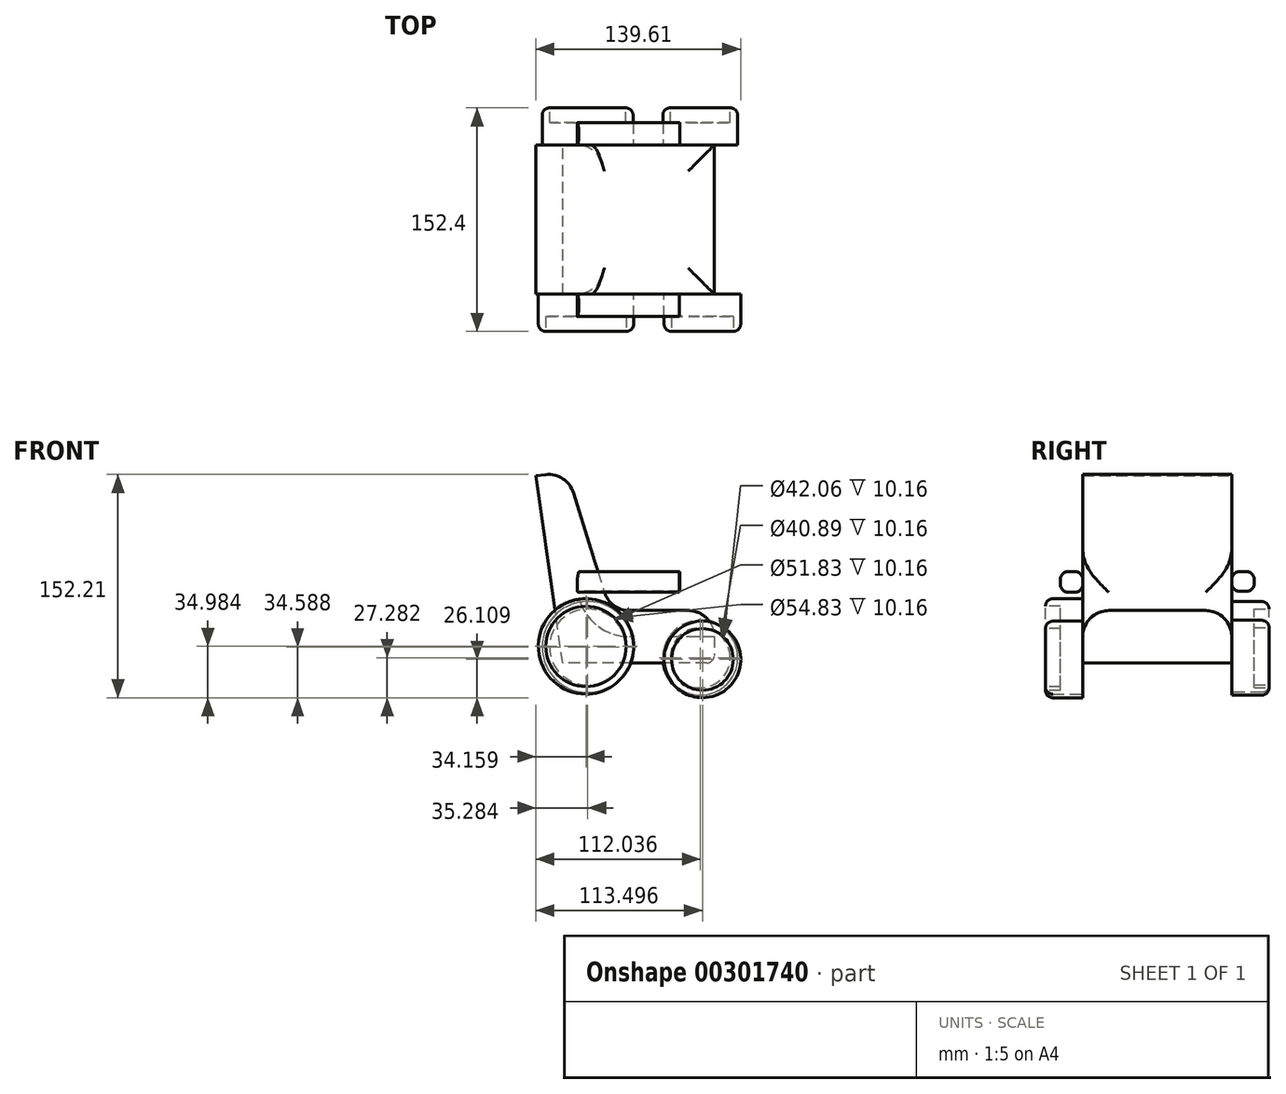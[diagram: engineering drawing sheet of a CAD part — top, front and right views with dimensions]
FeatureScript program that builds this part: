
annotation { "Feature Type Name" : "Feature", "Feature Type Description" : "" }
export const myFeature = defineFeature(function(context is Context, id is Id, definition is map)
    precondition{}
    {
        {
            var Q0;
            Q0=qCreatedBy(makeId("Front.planeOp"),FACE);
            var sketch = newSketch(context, id + "F0", { "sketchPlane" : qUnion([Q0])});
            skLineSegment(sketch, "E0", {"start": v(-41.82, 75.7) * mm, "end": v(-12.5, -18.42) * mm});
            skLineSegment(sketch, "E1", {"start": v(-12.5, -18.42) * mm, "end": v(58.5, -18.42) * mm});
            skLineSegment(sketch, "E2", {"start": v(58.5, -18.42) * mm, "end": v(58.5, -54.2) * mm});
            skLineSegment(sketch, "E3", {"start": v(58.5, -54.2) * mm, "end": v(-44.78, -54.2) * mm});
            skLineSegment(sketch, "E4", {"start": v(-44.78, -54.2) * mm, "end": v(-63.07, 73.56) * mm});
            skLineSegment(sketch, "E5", {"start": v(-63.07, 73.56) * mm, "end": v(-41.82, 75.7) * mm});
            skSolve(sketch);
        }
        {
            var Q0;
            Q0=makeQuery(id+"F0.imprint","IMPRINT",FACE,{"disambiguationData":[TD([[makeQuery(id+"F0.imprint","IMPRINT",EDGE,{"derivedFrom":sQuery(id+"F0.wireOp",EDGE,"E0")}),-1.0]])]});
            extrude(context, id + "F1", {"entities" : qUnion([Q0]), "depth" : 101.6 * mm});
        }
        {
            var Q0;
            Q0=makeQuery(id+"F1.opExtrude","SWEPT_EDGE",EDGE,{"disambiguationData":[OSD([sQuery(id+"F0.wireOp",EDGE,"E0"),sQuery(id+"F0.wireOp",EDGE,"E1")])]});
            var Q1;
            Q1=makeQuery(id+"F1.opExtrude","CAP_EDGE",EDGE,{"disambiguationData":[OSD([sQuery(id+"F0.wireOp",EDGE,"E1")])],"isStart":false});
            var Q2;
            Q2=makeQuery(id+"F1.opExtrude","CAP_EDGE",EDGE,{"disambiguationData":[OSD([sQuery(id+"F0.wireOp",EDGE,"E1")])],"isStart":true});
            var Q3;
            Q3=makeQuery(id+"F1.opExtrude","SWEPT_EDGE",EDGE,{"disambiguationData":[OSD([sQuery(id+"F0.wireOp",EDGE,"E1"),sQuery(id+"F0.wireOp",EDGE,"E2")])]});
            var Q4;
            Q4=makeQuery(id+"F1.opExtrude","SWEPT_EDGE",EDGE,{"disambiguationData":[OSD([sQuery(id+"F0.wireOp",EDGE,"E0"),sQuery(id+"F0.wireOp",EDGE,"E5")])]});
            fillet(context, id + "F2", {"entities" : qUnion([Q0, Q1, Q2, Q3, Q4]), "radius" : 17.78 * mm, "tangentPropagation" : true, "allowEdgeOverflow" : false});
        }
        {
            var Q0;
            Q0=qCreatedBy(makeId("Front.planeOp"),FACE);
            var sketch = newSketch(context, id + "F3", { "sketchPlane" : qUnion([Q0])});
            skCircle(sketch, "E6", {"center": v(-27.79, -43.3) * mm, "radius": 31 * mm});
            skCircle(sketch, "E7", {"center": v(48.97, -50.6) * mm, "radius": 25.53 * mm});
            skSolve(sketch);
        }
        {
            var Q0;
            Q0=makeQuery(id+"F3.imprint","IMPRINT",FACE,{"disambiguationData":[TD([[makeQuery(id+"F3.imprint","IMPRINT",EDGE,{"derivedFrom":sQuery(id+"F3.wireOp",EDGE,"E7")}),1.0]])]});
            var Q1;
            Q1=makeQuery(id+"F3.imprint","IMPRINT",FACE,{"disambiguationData":[TD([[makeQuery(id+"F3.imprint","IMPRINT",EDGE,{"derivedFrom":sQuery(id+"F3.wireOp",EDGE,"E6")}),1.0]])]});
            extrude(context, id + "F4", {"entities" : qUnion([Q0, Q1]), "operationType" : NewBodyOperationType.ADD, "oppositeDirection" : true, "depth" : 25.4 * mm});
        }
        {
            var Q0;
            Q0=makeQuery(id+"F1.opExtrude","CAP_FACE",FACE,{"disambiguationData":[OSD([sQuery(id+"F0.wireOp",EDGE,"E0"),sQuery(id+"F0.wireOp",EDGE,"E1"),sQuery(id+"F0.wireOp",EDGE,"E2"),sQuery(id+"F0.wireOp",EDGE,"E3"),sQuery(id+"F0.wireOp",EDGE,"E4"),sQuery(id+"F0.wireOp",EDGE,"E5")])],"isStart":false});
            var sketch = newSketch(context, id + "F5", { "sketchPlane" : qUnion([Q0])});
            skCircle(sketch, "E8", {"center": v(-28.91, -42.9) * mm, "radius": 32.5 * mm});
            skCircle(sketch, "E9", {"center": v(50.43, -51.77) * mm, "radius": 26.1 * mm});
            skSolve(sketch);
        }
        {
            var Q0;
            Q0 = qSketchRegion(id + "F5", true);
            extrude(context, id + "F6", {"entities" : qUnion([Q0]), "operationType" : NewBodyOperationType.ADD, "depth" : 25.4 * mm});
        }
        {
            var Q0;
            {var subQ1=sQuery(id+"F0.wireOp",EDGE,"E0");var subQ2=sQuery(id+"F0.wireOp",EDGE,"E5");var subQ3=sQuery(id+"F0.wireOp",EDGE,"E4");Q0=makeQuery(id+"F6.boolean.opBoolean","SPLIT",FACE,{"disambiguationData":[TD([makeQuery(id+"F1.opExtrude","SWEPT_FACE",FACE,{"disambiguationData":[OSD([subQ3])]})])],"derivedFrom":makeQuery(id+"F1.opExtrude","CAP_FACE",FACE,{"disambiguationData":[OSD([subQ1,sQuery(id+"F0.wireOp",EDGE,"E1"),sQuery(id+"F0.wireOp",EDGE,"E2"),sQuery(id+"F0.wireOp",EDGE,"E3"),subQ3,subQ2])],"isStart":false})});}
            var sketch = newSketch(context, id + "F7", { "sketchPlane" : qUnion([Q0])});
            skLineSegment(sketch, "E10.bottom", {"start": v(-47, 8) * mm, "end": v(34.84, 8) * mm});
            skLineSegment(sketch, "E10.top", {"start": v(-47, -5.87) * mm, "end": v(34.84, -5.87) * mm});
            skLineSegment(sketch, "E10.left", {"start": v(-47, 8) * mm, "end": v(-47, -5.87) * mm});
            skLineSegment(sketch, "E10.right", {"start": v(34.84, 8) * mm, "end": v(34.84, -5.87) * mm});
            skSolve(sketch);
        }
        {
            var Q0;
            {var subQ0=sQuery(id+"F7.wireOp",EDGE,"E10.right");Q0=makeQuery(id+"F7.imprint","IMPRINT",FACE,{"disambiguationData":[TD([[makeQuery(id+"F7.imprint","IMPRINT",EDGE,{"derivedFrom":subQ0}),-1.0]])]});}
            extrude(context, id + "F8", {"entities" : qUnion([Q0]), "depth" : 15.24 * mm});
        }
        {
            var Q0;
            Q0=makeQuery(id+"F8.opExtrude","CAP_EDGE",EDGE,{"disambiguationData":[OSD([sQuery(id+"F7.wireOp",EDGE,"E10.bottom")])],"isStart":false});
            var Q1;
            Q1=makeQuery(id+"F8.opExtrude","CAP_EDGE",EDGE,{"disambiguationData":[OSD([sQuery(id+"F7.wireOp",EDGE,"E10.top")])],"isStart":false});
            var Q2;
            Q2=makeQuery(id+"F8.opExtrude","CAP_EDGE",EDGE,{"disambiguationData":[OSD([sQuery(id+"F7.wireOp",EDGE,"E10.bottom")])],"isStart":true});
            fillet(context, id + "F9", {"entities" : qUnion([Q0, Q1, Q2]), "radius" : 5.08 * mm, "tangentPropagation" : true, "allowEdgeOverflow" : false});
        }
        {
            var Q0;
            {var subQ0=sQuery(id+"F0.wireOp",EDGE,"E5");var subQ1=sQuery(id+"F0.wireOp",EDGE,"E0");var subQ3=sQuery(id+"F0.wireOp",EDGE,"E1");var subQ4=sQuery(id+"F0.wireOp",EDGE,"E4");Q0=makeQuery(id+"F4.boolean.opBoolean","SPLIT",FACE,{"disambiguationData":[TD([makeQuery(id+"F1.opExtrude","SWEPT_FACE",FACE,{"disambiguationData":[OSD([subQ4])]})])],"derivedFrom":makeQuery(id+"F1.opExtrude","CAP_FACE",FACE,{"disambiguationData":[OSD([subQ1,subQ3,sQuery(id+"F0.wireOp",EDGE,"E2"),sQuery(id+"F0.wireOp",EDGE,"E3"),subQ4,subQ0])],"isStart":true})});}
            var sketch = newSketch(context, id + "F10", { "sketchPlane" : qUnion([Q0])});
            skLineSegment(sketch, "E11.bottom", {"start": v(-35.1, 8) * mm, "end": v(41.03, 8) * mm});
            skLineSegment(sketch, "E11.top", {"start": v(-35.1, -5.33) * mm, "end": v(41.03, -5.33) * mm});
            skLineSegment(sketch, "E11.left", {"start": v(-35.1, 8) * mm, "end": v(-35.1, -5.33) * mm});
            skLineSegment(sketch, "E11.right", {"start": v(41.03, 8) * mm, "end": v(41.03, -5.33) * mm});
            skSolve(sketch);
        }
        {
            var Q0;
            {var subQ0=sQuery(id+"F10.wireOp",EDGE,"E11.left");Q0=makeQuery(id+"F10.imprint","IMPRINT",FACE,{"disambiguationData":[TD([[makeQuery(id+"F10.imprint","IMPRINT",EDGE,{"derivedFrom":subQ0}),1.0]])]});}
            extrude(context, id + "F11", {"entities" : qUnion([Q0]), "depth" : 15.24 * mm});
        }
        {
            var Q0;
            Q0=makeQuery(id+"F11.opExtrude","CAP_EDGE",EDGE,{"disambiguationData":[OSD([sQuery(id+"F10.wireOp",EDGE,"E11.bottom")])],"isStart":false});
            var Q1;
            Q1=makeQuery(id+"F11.opExtrude","CAP_EDGE",EDGE,{"disambiguationData":[OSD([sQuery(id+"F10.wireOp",EDGE,"E11.bottom")])],"isStart":true});
            var Q2;
            Q2=makeQuery(id+"F11.opExtrude","CAP_EDGE",EDGE,{"disambiguationData":[OSD([sQuery(id+"F10.wireOp",EDGE,"E11.top")])],"isStart":false});
            var Q3;
            Q3=makeQuery(id+"F8.opExtrude","CAP_EDGE",EDGE,{"disambiguationData":[OSD([sQuery(id+"F7.wireOp",EDGE,"E10.top")])],"isStart":true});
            var Q4;
            Q4=makeQuery(id+"F11.opExtrude","CAP_EDGE",EDGE,{"disambiguationData":[OSD([sQuery(id+"F10.wireOp",EDGE,"E11.top")])],"isStart":true});
            fillet(context, id + "F12", {"entities" : qUnion([Q0, Q1, Q2, Q3, Q4]), "radius" : 5.08 * mm, "tangentPropagation" : true, "allowEdgeOverflow" : false});
        }
        {
            var Q0;
            Q0=makeQuery(id+"F6.opExtrude","CAP_EDGE",EDGE,{"disambiguationData":[OSD([sQuery(id+"F5.wireOp",EDGE,"E8")])],"isStart":false});
            var Q1;
            Q1=makeQuery(id+"F6.opExtrude","CAP_EDGE",EDGE,{"disambiguationData":[OSD([sQuery(id+"F5.wireOp",EDGE,"E9")])],"isStart":false});
            var Q2;
            Q2=makeQuery(id+"F4.opExtrude","CAP_EDGE",EDGE,{"disambiguationData":[OSD([sQuery(id+"F3.wireOp",EDGE,"E7")])],"isStart":false});
            var Q3;
            Q3=makeQuery(id+"F4.opExtrude","CAP_EDGE",EDGE,{"disambiguationData":[OSD([sQuery(id+"F3.wireOp",EDGE,"E6")])],"isStart":false});
            var Q4;
            Q4=makeQuery(id+"F1.opExtrude","SWEPT_EDGE",EDGE,{"disambiguationData":[OSD([sQuery(id+"F0.wireOp",EDGE,"E2"),sQuery(id+"F0.wireOp",EDGE,"E3")])]});
            fillet(context, id + "F13", {"entities" : qUnion([Q0, Q1, Q2, Q3, Q4]), "radius" : 5.08 * mm, "tangentPropagation" : true, "allowEdgeOverflow" : false});
        }
        {
            var Q0;
            Q0=makeQuery(id+"F6.opExtrude","CAP_FACE",FACE,{"disambiguationData":[OSD([sQuery(id+"F5.wireOp",EDGE,"E9")])],"isStart":false});
            extrude(context, id + "F14", {"entities" : qUnion([Q0]), "operationType" : NewBodyOperationType.REMOVE, "oppositeDirection" : true, "depth" : 10.16 * mm});
        }
        {
            var Q0;
            Q0=makeQuery(id+"F4.opExtrude","CAP_FACE",FACE,{"disambiguationData":[OSD([sQuery(id+"F3.wireOp",EDGE,"E7")])],"isStart":false});
            var Q1;
            Q1=makeQuery(id+"F4.opExtrude","CAP_FACE",FACE,{"disambiguationData":[OSD([sQuery(id+"F3.wireOp",EDGE,"E6")])],"isStart":false});
            extrude(context, id + "F15", {"entities" : qUnion([Q0, Q1]), "operationType" : NewBodyOperationType.REMOVE, "oppositeDirection" : true, "depth" : 10.16 * mm});
        }
        {
            var Q0;
            Q0=makeQuery(id+"F6.opExtrude","CAP_FACE",FACE,{"disambiguationData":[OSD([sQuery(id+"F5.wireOp",EDGE,"E8")])],"isStart":false});
            extrude(context, id + "F16", {"entities" : qUnion([Q0]), "operationType" : NewBodyOperationType.REMOVE, "oppositeDirection" : true, "depth" : 10.16 * mm});
        }
    });
